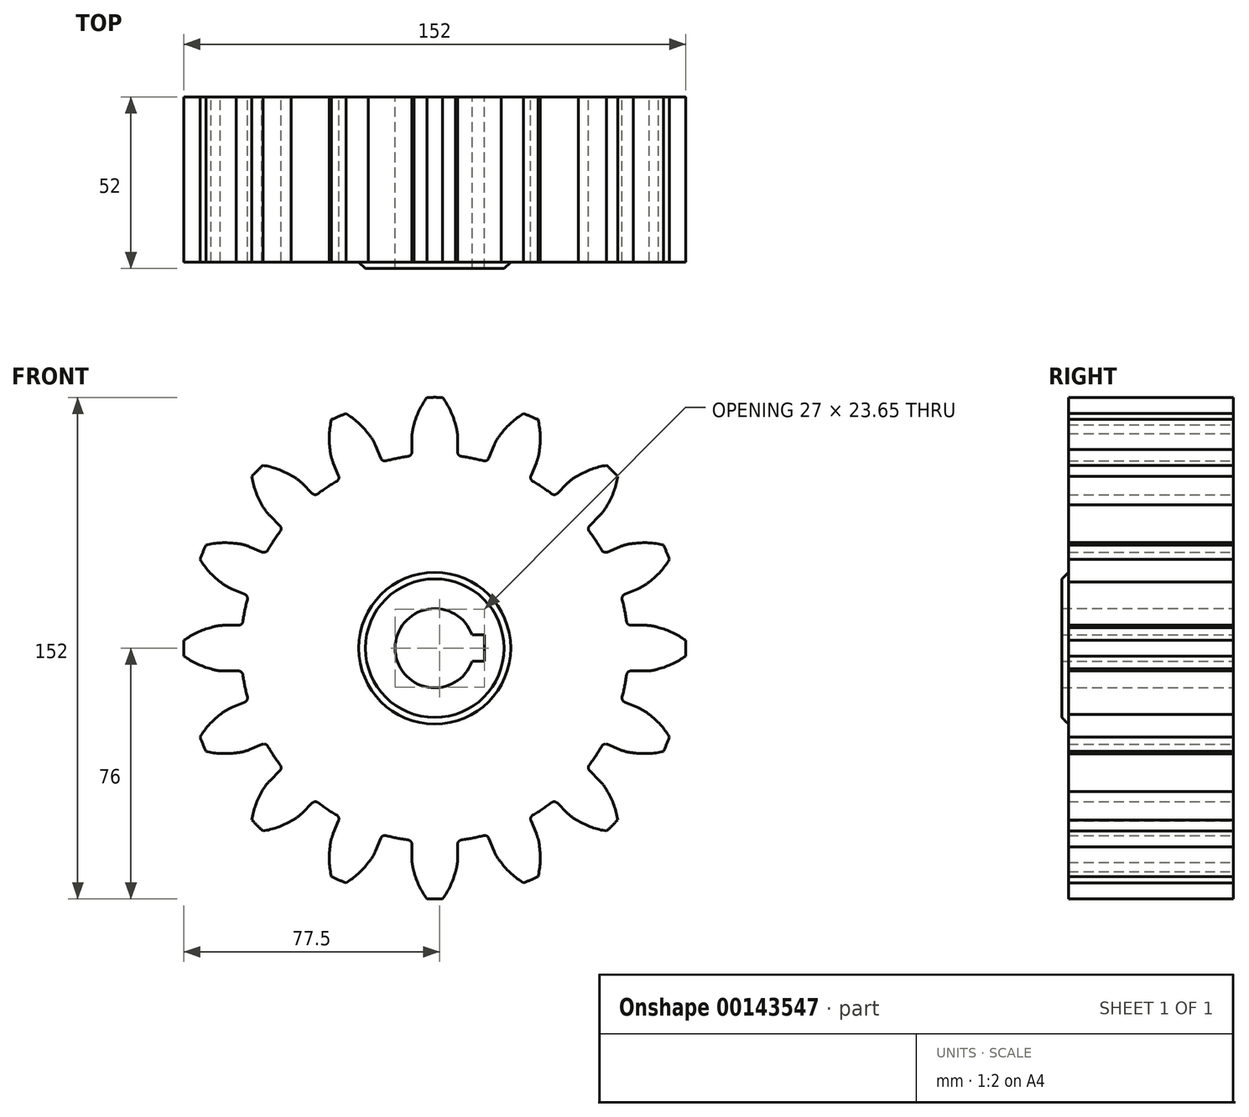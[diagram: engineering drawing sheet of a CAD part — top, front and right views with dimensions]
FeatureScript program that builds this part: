
annotation { "Feature Type Name" : "Feature", "Feature Type Description" : "" }
export const myFeature = defineFeature(function(context is Context, id is Id, definition is map)
    precondition{}
    {
        {
            var Q0;
            Q0=qCreatedBy(makeId("Front.planeOp"),FACE);
            var sketch = newSketch(context, id + "F0", { "sketchPlane" : qUnion([Q0])});
            skArc(sketch, "E0", {"start": v(-52.04, 55.39) * mm, "mid": v(-53.74, 53.74) * mm, "end": v(-55.39, 52.04) * mm});
            skArc(sketch, "E1", {"start": v(-8.06, 58.1) * mm, "mid": v(-11.44, 57.53) * mm, "end": v(-14.78, 56.77) * mm});
            skLineSegment(sketch, "E2", {"start": v(6.92, 59.42) * mm, "end": v(6.92, 63.63) * mm});
            skArc(sketch, "E3", {"start": v(6.92, 63.63) * mm, "mid": v(6.77, 65.7) * mm, "end": v(6.28, 67.7) * mm});
            skArc(sketch, "E4", {"start": v(6.28, 67.7) * mm, "mid": v(4.72, 72.02) * mm, "end": v(2.37, 75.96) * mm});
            skLineSegment(sketch, "E5", {"start": v(0, 0) * mm, "end": v(0, 104.76) * mm, "construction": true});
            skArc(sketch, "E6.MirrorCS", {"start": v(-6.28, 67.7) * mm, "mid": v(-4.72, 72.02) * mm, "end": v(-2.37, 75.96) * mm});
            skArc(sketch, "E7.MirrorCS", {"start": v(-6.92, 63.63) * mm, "mid": v(-6.77, 65.7) * mm, "end": v(-6.28, 67.7) * mm});
            skLineSegment(sketch, "E8.MirrorCS", {"start": v(-6.92, 59.42) * mm, "end": v(-6.92, 63.63) * mm});
            skPoint(sketch, "E9.visualSharp", {"position": v(6.92, 58.25) * mm});
            skArc(sketch, "E9.filletArc", {"start": v(6.92, 59.42) * mm, "mid": v(7.24, 58.55) * mm, "end": v(8.06, 58.1) * mm});
            skPoint(sketch, "E10.visualSharp", {"position": v(-6.92, 58.25) * mm});
            skArc(sketch, "E10.filletArc", {"start": v(-8.06, 58.1) * mm, "mid": v(-7.24, 58.55) * mm, "end": v(-6.92, 59.42) * mm});
            skArc(sketch, "E11.1.0", {"start": v(31.71, 60.15) * mm, "mid": v(31.92, 64.74) * mm, "end": v(31.26, 69.28) * mm});
            skArc(sketch, "E11.1.1", {"start": v(20.1, 64.96) * mm, "mid": v(23.2, 68.35) * mm, "end": v(26.88, 71.09) * mm});
            skArc(sketch, "E11.1.2", {"start": v(30.74, 56.13) * mm, "mid": v(31.4, 58.1) * mm, "end": v(31.71, 60.15) * mm});
            skArc(sketch, "E11.1.3", {"start": v(17.96, 61.43) * mm, "mid": v(18.89, 63.28) * mm, "end": v(20.1, 64.96) * mm});
            skLineSegment(sketch, "E11.1.4", {"start": v(16.35, 57.54) * mm, "end": v(17.96, 61.43) * mm});
            skLineSegment(sketch, "E11.1.5", {"start": v(29.13, 52.25) * mm, "end": v(30.74, 56.13) * mm});
            skArc(sketch, "E11.1.6", {"start": v(29.13, 52.25) * mm, "mid": v(29.1, 51.32) * mm, "end": v(29.69, 50.6) * mm});
            skArc(sketch, "E11.1.7", {"start": v(14.78, 56.77) * mm, "mid": v(15.71, 56.86) * mm, "end": v(16.35, 57.54) * mm});
            skArc(sketch, "E11.2.0", {"start": v(52.32, 43.44) * mm, "mid": v(54.26, 47.6) * mm, "end": v(55.39, 52.04) * mm});
            skArc(sketch, "E11.2.1", {"start": v(43.44, 52.32) * mm, "mid": v(47.6, 54.26) * mm, "end": v(52.04, 55.39) * mm});
            skArc(sketch, "E11.2.2", {"start": v(49.88, 40.1) * mm, "mid": v(51.24, 41.67) * mm, "end": v(52.32, 43.44) * mm});
            skArc(sketch, "E11.2.3", {"start": v(40.1, 49.88) * mm, "mid": v(41.67, 51.24) * mm, "end": v(43.44, 52.32) * mm});
            skLineSegment(sketch, "E11.2.4", {"start": v(37.13, 46.9) * mm, "end": v(40.1, 49.88) * mm});
            skLineSegment(sketch, "E11.2.5", {"start": v(46.9, 37.13) * mm, "end": v(49.88, 40.1) * mm});
            skArc(sketch, "E11.2.6", {"start": v(46.9, 37.13) * mm, "mid": v(46.52, 36.28) * mm, "end": v(46.79, 35.38) * mm});
            skArc(sketch, "E11.2.7", {"start": v(35.38, 46.79) * mm, "mid": v(36.28, 46.52) * mm, "end": v(37.13, 46.9) * mm});
            skArc(sketch, "E11.3.0", {"start": v(64.96, 20.1) * mm, "mid": v(68.35, 23.2) * mm, "end": v(71.09, 26.88) * mm});
            skArc(sketch, "E11.3.1", {"start": v(60.15, 31.71) * mm, "mid": v(64.74, 31.92) * mm, "end": v(69.28, 31.26) * mm});
            skArc(sketch, "E11.3.2", {"start": v(61.43, 17.96) * mm, "mid": v(63.28, 18.89) * mm, "end": v(64.96, 20.1) * mm});
            skArc(sketch, "E11.3.3", {"start": v(56.13, 30.74) * mm, "mid": v(58.1, 31.4) * mm, "end": v(60.15, 31.71) * mm});
            skLineSegment(sketch, "E11.3.4", {"start": v(52.25, 29.13) * mm, "end": v(56.13, 30.74) * mm});
            skLineSegment(sketch, "E11.3.5", {"start": v(57.54, 16.35) * mm, "end": v(61.43, 17.96) * mm});
            skArc(sketch, "E11.3.6", {"start": v(57.54, 16.35) * mm, "mid": v(56.86, 15.71) * mm, "end": v(56.77, 14.78) * mm});
            skArc(sketch, "E11.3.7", {"start": v(50.6, 29.69) * mm, "mid": v(51.32, 29.1) * mm, "end": v(52.25, 29.13) * mm});
            skArc(sketch, "E11.4.0", {"start": v(67.7, -6.28) * mm, "mid": v(72.02, -4.72) * mm, "end": v(75.96, -2.37) * mm});
            skArc(sketch, "E11.4.1", {"start": v(67.7, 6.28) * mm, "mid": v(72.02, 4.72) * mm, "end": v(75.96, 2.37) * mm});
            skArc(sketch, "E11.4.2", {"start": v(63.63, -6.92) * mm, "mid": v(65.7, -6.77) * mm, "end": v(67.7, -6.28) * mm});
            skArc(sketch, "E11.4.3", {"start": v(63.63, 6.92) * mm, "mid": v(65.7, 6.77) * mm, "end": v(67.7, 6.28) * mm});
            skLineSegment(sketch, "E11.4.4", {"start": v(59.42, 6.92) * mm, "end": v(63.63, 6.92) * mm});
            skLineSegment(sketch, "E11.4.5", {"start": v(59.42, -6.92) * mm, "end": v(63.63, -6.92) * mm});
            skArc(sketch, "E11.4.6", {"start": v(59.42, -6.92) * mm, "mid": v(58.55, -7.24) * mm, "end": v(58.1, -8.06) * mm});
            skArc(sketch, "E11.4.7", {"start": v(58.1, 8.06) * mm, "mid": v(58.55, 7.24) * mm, "end": v(59.42, 6.92) * mm});
            skArc(sketch, "E11.5.0", {"start": v(60.15, -31.71) * mm, "mid": v(64.74, -31.92) * mm, "end": v(69.28, -31.26) * mm});
            skArc(sketch, "E11.5.1", {"start": v(64.96, -20.1) * mm, "mid": v(68.35, -23.2) * mm, "end": v(71.09, -26.88) * mm});
            skArc(sketch, "E11.5.2", {"start": v(56.13, -30.74) * mm, "mid": v(58.1, -31.4) * mm, "end": v(60.15, -31.71) * mm});
            skArc(sketch, "E11.5.3", {"start": v(61.43, -17.96) * mm, "mid": v(63.28, -18.89) * mm, "end": v(64.96, -20.1) * mm});
            skLineSegment(sketch, "E11.5.4", {"start": v(57.54, -16.35) * mm, "end": v(61.43, -17.96) * mm});
            skLineSegment(sketch, "E11.5.5", {"start": v(52.25, -29.13) * mm, "end": v(56.13, -30.74) * mm});
            skArc(sketch, "E11.5.6", {"start": v(52.25, -29.13) * mm, "mid": v(51.32, -29.1) * mm, "end": v(50.6, -29.69) * mm});
            skArc(sketch, "E11.5.7", {"start": v(56.77, -14.78) * mm, "mid": v(56.86, -15.71) * mm, "end": v(57.54, -16.35) * mm});
            skArc(sketch, "E11.6.0", {"start": v(43.44, -52.32) * mm, "mid": v(47.6, -54.26) * mm, "end": v(52.04, -55.39) * mm});
            skArc(sketch, "E11.6.1", {"start": v(52.32, -43.44) * mm, "mid": v(54.26, -47.6) * mm, "end": v(55.39, -52.04) * mm});
            skArc(sketch, "E11.6.2", {"start": v(40.1, -49.88) * mm, "mid": v(41.67, -51.24) * mm, "end": v(43.44, -52.32) * mm});
            skArc(sketch, "E11.6.3", {"start": v(49.88, -40.1) * mm, "mid": v(51.24, -41.67) * mm, "end": v(52.32, -43.44) * mm});
            skLineSegment(sketch, "E11.6.4", {"start": v(46.9, -37.13) * mm, "end": v(49.88, -40.1) * mm});
            skLineSegment(sketch, "E11.6.5", {"start": v(37.13, -46.9) * mm, "end": v(40.1, -49.88) * mm});
            skArc(sketch, "E11.6.6", {"start": v(37.13, -46.9) * mm, "mid": v(36.28, -46.52) * mm, "end": v(35.38, -46.79) * mm});
            skArc(sketch, "E11.6.7", {"start": v(46.79, -35.38) * mm, "mid": v(46.52, -36.28) * mm, "end": v(46.9, -37.13) * mm});
            skArc(sketch, "E11.7.0", {"start": v(20.1, -64.96) * mm, "mid": v(23.2, -68.35) * mm, "end": v(26.88, -71.09) * mm});
            skArc(sketch, "E11.7.1", {"start": v(31.71, -60.15) * mm, "mid": v(31.92, -64.74) * mm, "end": v(31.26, -69.28) * mm});
            skArc(sketch, "E11.7.2", {"start": v(17.96, -61.43) * mm, "mid": v(18.89, -63.28) * mm, "end": v(20.1, -64.96) * mm});
            skArc(sketch, "E11.7.3", {"start": v(30.74, -56.13) * mm, "mid": v(31.4, -58.1) * mm, "end": v(31.71, -60.15) * mm});
            skLineSegment(sketch, "E11.7.4", {"start": v(29.13, -52.25) * mm, "end": v(30.74, -56.13) * mm});
            skLineSegment(sketch, "E11.7.5", {"start": v(16.35, -57.54) * mm, "end": v(17.96, -61.43) * mm});
            skArc(sketch, "E11.7.6", {"start": v(16.35, -57.54) * mm, "mid": v(15.71, -56.86) * mm, "end": v(14.78, -56.77) * mm});
            skArc(sketch, "E11.7.7", {"start": v(29.69, -50.6) * mm, "mid": v(29.1, -51.32) * mm, "end": v(29.13, -52.25) * mm});
            skArc(sketch, "E11.8.0", {"start": v(-6.28, -67.7) * mm, "mid": v(-4.72, -72.02) * mm, "end": v(-2.37, -75.96) * mm});
            skArc(sketch, "E11.8.1", {"start": v(6.28, -67.7) * mm, "mid": v(4.72, -72.02) * mm, "end": v(2.37, -75.96) * mm});
            skArc(sketch, "E11.8.2", {"start": v(-6.92, -63.63) * mm, "mid": v(-6.77, -65.7) * mm, "end": v(-6.28, -67.7) * mm});
            skArc(sketch, "E11.8.3", {"start": v(6.92, -63.63) * mm, "mid": v(6.77, -65.7) * mm, "end": v(6.28, -67.7) * mm});
            skLineSegment(sketch, "E11.8.4", {"start": v(6.92, -59.42) * mm, "end": v(6.92, -63.63) * mm});
            skLineSegment(sketch, "E11.8.5", {"start": v(-6.92, -59.42) * mm, "end": v(-6.92, -63.63) * mm});
            skArc(sketch, "E11.8.6", {"start": v(-6.92, -59.42) * mm, "mid": v(-7.24, -58.55) * mm, "end": v(-8.06, -58.1) * mm});
            skArc(sketch, "E11.8.7", {"start": v(8.06, -58.1) * mm, "mid": v(7.24, -58.55) * mm, "end": v(6.92, -59.42) * mm});
            skArc(sketch, "E11.9.0", {"start": v(-31.71, -60.15) * mm, "mid": v(-31.92, -64.74) * mm, "end": v(-31.26, -69.28) * mm});
            skArc(sketch, "E11.9.1", {"start": v(-20.1, -64.96) * mm, "mid": v(-23.2, -68.35) * mm, "end": v(-26.88, -71.09) * mm});
            skArc(sketch, "E11.9.2", {"start": v(-30.74, -56.13) * mm, "mid": v(-31.4, -58.1) * mm, "end": v(-31.71, -60.15) * mm});
            skArc(sketch, "E11.9.3", {"start": v(-17.96, -61.43) * mm, "mid": v(-18.89, -63.28) * mm, "end": v(-20.1, -64.96) * mm});
            skLineSegment(sketch, "E11.9.4", {"start": v(-16.35, -57.54) * mm, "end": v(-17.96, -61.43) * mm});
            skLineSegment(sketch, "E11.9.5", {"start": v(-29.13, -52.25) * mm, "end": v(-30.74, -56.13) * mm});
            skArc(sketch, "E11.9.6", {"start": v(-29.13, -52.25) * mm, "mid": v(-29.1, -51.32) * mm, "end": v(-29.69, -50.6) * mm});
            skArc(sketch, "E11.9.7", {"start": v(-14.78, -56.77) * mm, "mid": v(-15.71, -56.86) * mm, "end": v(-16.35, -57.54) * mm});
            skArc(sketch, "E11.10.0", {"start": v(-52.32, -43.44) * mm, "mid": v(-54.26, -47.6) * mm, "end": v(-55.39, -52.04) * mm});
            skArc(sketch, "E11.10.1", {"start": v(-43.44, -52.32) * mm, "mid": v(-47.6, -54.26) * mm, "end": v(-52.04, -55.39) * mm});
            skArc(sketch, "E11.10.2", {"start": v(-49.88, -40.1) * mm, "mid": v(-51.24, -41.67) * mm, "end": v(-52.32, -43.44) * mm});
            skArc(sketch, "E11.10.3", {"start": v(-40.1, -49.88) * mm, "mid": v(-41.67, -51.24) * mm, "end": v(-43.44, -52.32) * mm});
            skLineSegment(sketch, "E11.10.4", {"start": v(-37.13, -46.9) * mm, "end": v(-40.1, -49.88) * mm});
            skLineSegment(sketch, "E11.10.5", {"start": v(-46.9, -37.13) * mm, "end": v(-49.88, -40.1) * mm});
            skArc(sketch, "E11.10.6", {"start": v(-46.9, -37.13) * mm, "mid": v(-46.52, -36.28) * mm, "end": v(-46.79, -35.38) * mm});
            skArc(sketch, "E11.10.7", {"start": v(-35.38, -46.79) * mm, "mid": v(-36.28, -46.52) * mm, "end": v(-37.13, -46.9) * mm});
            skArc(sketch, "E11.11.0", {"start": v(-64.96, -20.1) * mm, "mid": v(-68.35, -23.2) * mm, "end": v(-71.09, -26.88) * mm});
            skArc(sketch, "E11.11.1", {"start": v(-60.15, -31.71) * mm, "mid": v(-64.74, -31.92) * mm, "end": v(-69.28, -31.26) * mm});
            skArc(sketch, "E11.11.2", {"start": v(-61.43, -17.96) * mm, "mid": v(-63.28, -18.89) * mm, "end": v(-64.96, -20.1) * mm});
            skArc(sketch, "E11.11.3", {"start": v(-56.13, -30.74) * mm, "mid": v(-58.1, -31.4) * mm, "end": v(-60.15, -31.71) * mm});
            skLineSegment(sketch, "E11.11.4", {"start": v(-52.25, -29.13) * mm, "end": v(-56.13, -30.74) * mm});
            skLineSegment(sketch, "E11.11.5", {"start": v(-57.54, -16.35) * mm, "end": v(-61.43, -17.96) * mm});
            skArc(sketch, "E11.11.6", {"start": v(-57.54, -16.35) * mm, "mid": v(-56.86, -15.71) * mm, "end": v(-56.77, -14.78) * mm});
            skArc(sketch, "E11.11.7", {"start": v(-50.6, -29.69) * mm, "mid": v(-51.32, -29.1) * mm, "end": v(-52.25, -29.13) * mm});
            skArc(sketch, "E11.12.0", {"start": v(-67.7, 6.28) * mm, "mid": v(-72.02, 4.72) * mm, "end": v(-75.96, 2.37) * mm});
            skArc(sketch, "E11.12.1", {"start": v(-67.7, -6.28) * mm, "mid": v(-72.02, -4.72) * mm, "end": v(-75.96, -2.37) * mm});
            skArc(sketch, "E11.12.2", {"start": v(-63.63, 6.92) * mm, "mid": v(-65.7, 6.77) * mm, "end": v(-67.7, 6.28) * mm});
            skArc(sketch, "E11.12.3", {"start": v(-63.63, -6.92) * mm, "mid": v(-65.7, -6.77) * mm, "end": v(-67.7, -6.28) * mm});
            skLineSegment(sketch, "E11.12.4", {"start": v(-59.42, -6.92) * mm, "end": v(-63.63, -6.92) * mm});
            skLineSegment(sketch, "E11.12.5", {"start": v(-59.42, 6.92) * mm, "end": v(-63.63, 6.92) * mm});
            skArc(sketch, "E11.12.6", {"start": v(-59.42, 6.92) * mm, "mid": v(-58.55, 7.24) * mm, "end": v(-58.1, 8.06) * mm});
            skArc(sketch, "E11.12.7", {"start": v(-58.1, -8.06) * mm, "mid": v(-58.55, -7.24) * mm, "end": v(-59.42, -6.92) * mm});
            skArc(sketch, "E11.13.0", {"start": v(-60.15, 31.71) * mm, "mid": v(-64.74, 31.92) * mm, "end": v(-69.28, 31.26) * mm});
            skArc(sketch, "E11.13.1", {"start": v(-64.96, 20.1) * mm, "mid": v(-68.35, 23.2) * mm, "end": v(-71.09, 26.88) * mm});
            skArc(sketch, "E11.13.2", {"start": v(-56.13, 30.74) * mm, "mid": v(-58.1, 31.4) * mm, "end": v(-60.15, 31.71) * mm});
            skArc(sketch, "E11.13.3", {"start": v(-61.43, 17.96) * mm, "mid": v(-63.28, 18.89) * mm, "end": v(-64.96, 20.1) * mm});
            skLineSegment(sketch, "E11.13.4", {"start": v(-57.54, 16.35) * mm, "end": v(-61.43, 17.96) * mm});
            skLineSegment(sketch, "E11.13.5", {"start": v(-52.25, 29.13) * mm, "end": v(-56.13, 30.74) * mm});
            skArc(sketch, "E11.13.6", {"start": v(-52.25, 29.13) * mm, "mid": v(-51.32, 29.1) * mm, "end": v(-50.6, 29.69) * mm});
            skArc(sketch, "E11.13.7", {"start": v(-56.77, 14.78) * mm, "mid": v(-56.86, 15.71) * mm, "end": v(-57.54, 16.35) * mm});
            skArc(sketch, "E11.14.0", {"start": v(-43.44, 52.32) * mm, "mid": v(-47.6, 54.26) * mm, "end": v(-52.04, 55.39) * mm});
            skArc(sketch, "E11.14.1", {"start": v(-52.32, 43.44) * mm, "mid": v(-54.26, 47.6) * mm, "end": v(-55.39, 52.04) * mm});
            skArc(sketch, "E11.14.2", {"start": v(-40.1, 49.88) * mm, "mid": v(-41.67, 51.24) * mm, "end": v(-43.44, 52.32) * mm});
            skArc(sketch, "E11.14.3", {"start": v(-49.88, 40.1) * mm, "mid": v(-51.24, 41.67) * mm, "end": v(-52.32, 43.44) * mm});
            skLineSegment(sketch, "E11.14.4", {"start": v(-46.9, 37.13) * mm, "end": v(-49.88, 40.1) * mm});
            skLineSegment(sketch, "E11.14.5", {"start": v(-37.13, 46.9) * mm, "end": v(-40.1, 49.88) * mm});
            skArc(sketch, "E11.14.6", {"start": v(-37.13, 46.9) * mm, "mid": v(-36.28, 46.52) * mm, "end": v(-35.38, 46.79) * mm});
            skArc(sketch, "E11.14.7", {"start": v(-46.79, 35.38) * mm, "mid": v(-46.52, 36.28) * mm, "end": v(-46.9, 37.13) * mm});
            skArc(sketch, "E11.15.0", {"start": v(-20.1, 64.96) * mm, "mid": v(-23.2, 68.35) * mm, "end": v(-26.88, 71.09) * mm});
            skArc(sketch, "E11.15.1", {"start": v(-31.71, 60.15) * mm, "mid": v(-31.92, 64.74) * mm, "end": v(-31.26, 69.28) * mm});
            skArc(sketch, "E11.15.2", {"start": v(-17.96, 61.43) * mm, "mid": v(-18.89, 63.28) * mm, "end": v(-20.1, 64.96) * mm});
            skArc(sketch, "E11.15.3", {"start": v(-30.74, 56.13) * mm, "mid": v(-31.4, 58.1) * mm, "end": v(-31.71, 60.15) * mm});
            skLineSegment(sketch, "E11.15.4", {"start": v(-29.13, 52.25) * mm, "end": v(-30.74, 56.13) * mm});
            skLineSegment(sketch, "E11.15.5", {"start": v(-16.35, 57.54) * mm, "end": v(-17.96, 61.43) * mm});
            skArc(sketch, "E11.15.6", {"start": v(-16.35, 57.54) * mm, "mid": v(-15.71, 56.86) * mm, "end": v(-14.78, 56.77) * mm});
            skArc(sketch, "E11.15.7", {"start": v(-29.69, 50.6) * mm, "mid": v(-29.1, 51.32) * mm, "end": v(-29.13, 52.25) * mm});
            skLineSegment(sketch, "E11.anchor1", {"start": v(0, 0) * mm, "end": v(-8.06, 58.1) * mm, "construction": true});
            skLineSegment(sketch, "E11.anchor2", {"start": v(0, 0) * mm, "end": v(-8.06, 58.1) * mm, "construction": true});
            skArc(sketch, "E12.trimOffspring", {"start": v(-29.69, 50.6) * mm, "mid": v(-32.59, 48.77) * mm, "end": v(-35.38, 46.79) * mm});
            skArc(sketch, "E13.trimOffspring", {"start": v(14.78, 56.77) * mm, "mid": v(11.44, 57.53) * mm, "end": v(8.06, 58.1) * mm});
            skArc(sketch, "E14.trimOffspring", {"start": v(35.38, 46.79) * mm, "mid": v(32.59, 48.77) * mm, "end": v(29.69, 50.6) * mm});
            skArc(sketch, "E15.trimOffspring", {"start": v(-46.79, 35.38) * mm, "mid": v(-48.77, 32.59) * mm, "end": v(-50.6, 29.69) * mm});
            skArc(sketch, "E16.trimOffspring", {"start": v(50.6, 29.69) * mm, "mid": v(48.77, 32.59) * mm, "end": v(46.79, 35.38) * mm});
            skArc(sketch, "E17.trimOffspring", {"start": v(58.1, 8.06) * mm, "mid": v(57.53, 11.44) * mm, "end": v(56.77, 14.78) * mm});
            skArc(sketch, "E18.trimOffspring", {"start": v(56.77, -14.78) * mm, "mid": v(57.53, -11.44) * mm, "end": v(58.1, -8.06) * mm});
            skArc(sketch, "E19.trimOffspring", {"start": v(-56.77, 14.78) * mm, "mid": v(-57.53, 11.44) * mm, "end": v(-58.1, 8.06) * mm});
            skArc(sketch, "E20.trimOffspring", {"start": v(-58.1, -8.06) * mm, "mid": v(-57.53, -11.44) * mm, "end": v(-56.77, -14.78) * mm});
            skArc(sketch, "E21.trimOffspring", {"start": v(-50.6, -29.69) * mm, "mid": v(-48.77, -32.59) * mm, "end": v(-46.79, -35.38) * mm});
            skArc(sketch, "E22.trimOffspring", {"start": v(-35.38, -46.79) * mm, "mid": v(-32.59, -48.77) * mm, "end": v(-29.69, -50.6) * mm});
            skArc(sketch, "E23.trimOffspring", {"start": v(-14.78, -56.77) * mm, "mid": v(-11.44, -57.53) * mm, "end": v(-8.06, -58.1) * mm});
            skArc(sketch, "E24.trimOffspring", {"start": v(8.06, -58.1) * mm, "mid": v(11.44, -57.53) * mm, "end": v(14.78, -56.77) * mm});
            skArc(sketch, "E25.trimOffspring", {"start": v(29.69, -50.6) * mm, "mid": v(32.59, -48.77) * mm, "end": v(35.38, -46.79) * mm});
            skArc(sketch, "E26.trimOffspring", {"start": v(46.79, -35.38) * mm, "mid": v(48.77, -32.59) * mm, "end": v(50.6, -29.69) * mm});
            skArc(sketch, "E27.trimOffspring", {"start": v(-26.88, 71.09) * mm, "mid": v(-29.08, 70.21) * mm, "end": v(-31.26, 69.28) * mm});
            skArc(sketch, "E28.trimOffspring", {"start": v(-75.96, 2.37) * mm, "mid": v(-76, 0) * mm, "end": v(-75.96, -2.37) * mm});
            skArc(sketch, "E29.trimOffspring", {"start": v(-55.39, -52.04) * mm, "mid": v(-53.74, -53.74) * mm, "end": v(-52.04, -55.39) * mm});
            skArc(sketch, "E30.trimOffspring", {"start": v(-71.09, -26.88) * mm, "mid": v(-70.21, -29.08) * mm, "end": v(-69.28, -31.26) * mm});
            skArc(sketch, "E31.trimOffspring", {"start": v(-2.37, -75.96) * mm, "mid": v(0, -76) * mm, "end": v(2.37, -75.96) * mm});
            skArc(sketch, "E32.trimOffspring", {"start": v(52.04, -55.39) * mm, "mid": v(53.74, -53.74) * mm, "end": v(55.39, -52.04) * mm});
            skArc(sketch, "E33.trimOffspring", {"start": v(26.88, -71.09) * mm, "mid": v(29.08, -70.21) * mm, "end": v(31.26, -69.28) * mm});
            skArc(sketch, "E34.trimOffspring", {"start": v(75.96, -2.37) * mm, "mid": v(76, 0) * mm, "end": v(75.96, 2.37) * mm});
            skArc(sketch, "E35.trimOffspring", {"start": v(55.39, 52.04) * mm, "mid": v(53.74, 53.74) * mm, "end": v(52.04, 55.39) * mm});
            skArc(sketch, "E36.trimOffspring", {"start": v(2.37, 75.96) * mm, "mid": v(0, 76) * mm, "end": v(-2.37, 75.96) * mm});
            skArc(sketch, "E37.trimOffspring", {"start": v(31.26, 69.28) * mm, "mid": v(29.08, 70.21) * mm, "end": v(26.88, 71.09) * mm});
            skArc(sketch, "E38", {"start": v(71.09, 26.88) * mm, "mid": v(70.21, 29.08) * mm, "end": v(69.28, 31.26) * mm});
            skArc(sketch, "E39", {"start": v(69.28, -31.26) * mm, "mid": v(70.21, -29.08) * mm, "end": v(71.09, -26.88) * mm});
            skArc(sketch, "E40", {"start": v(-69.28, 31.26) * mm, "mid": v(-70.21, 29.08) * mm, "end": v(-71.09, 26.88) * mm});
            skArc(sketch, "E41", {"start": v(-26.88, -71.09) * mm, "mid": v(-29.08, -70.21) * mm, "end": v(-31.26, -69.28) * mm});
            skArc(sketch, "E42", {"start": v(11.31, 4) * mm, "mid": v(-12, 0) * mm, "end": v(11.31, -4) * mm});
            skLineSegment(sketch, "E43", {"start": v(-12, 0) * mm, "end": v(0, 0) * mm});
            skLineSegment(sketch, "E44", {"start": v(15, 0) * mm, "end": v(15, 4) * mm});
            skLineSegment(sketch, "E45", {"start": v(15, 4) * mm, "end": v(11.31, 4) * mm});
            skLineSegment(sketch, "E46", {"start": v(15, 0) * mm, "end": v(15, -4) * mm});
            skLineSegment(sketch, "E47", {"start": v(15, -4) * mm, "end": v(11.31, -4) * mm});
            skSolve(sketch);
        }
        {
            var Q0;
            Q0 = qSketchRegion(id + "F0", true);
            extrude(context, id + "F1", {"entities" : qUnion([Q0]), "endBound" : BoundingType.SYMMETRIC, "depth" : 50 * mm});
        }
        {
            var Q0;
            Q0=makeQuery(id+"F1.opExtrude","CAP_FACE",FACE,{"disambiguationData":[OSD([sQuery(id+"F0.wireOp",EDGE,"E0"),sQuery(id+"F0.wireOp",EDGE,"E1"),sQuery(id+"F0.wireOp",EDGE,"E11.1.0"),sQuery(id+"F0.wireOp",EDGE,"E11.1.1"),sQuery(id+"F0.wireOp",EDGE,"E11.1.2"),sQuery(id+"F0.wireOp",EDGE,"E11.1.3"),sQuery(id+"F0.wireOp",EDGE,"E11.1.4"),sQuery(id+"F0.wireOp",EDGE,"E11.1.5"),sQuery(id+"F0.wireOp",EDGE,"E11.1.6"),sQuery(id+"F0.wireOp",EDGE,"E11.1.7"),sQuery(id+"F0.wireOp",EDGE,"E11.2.0"),sQuery(id+"F0.wireOp",EDGE,"E11.2.1"),sQuery(id+"F0.wireOp",EDGE,"E11.2.2"),sQuery(id+"F0.wireOp",EDGE,"E11.2.3"),sQuery(id+"F0.wireOp",EDGE,"E11.2.4"),sQuery(id+"F0.wireOp",EDGE,"E11.2.5"),sQuery(id+"F0.wireOp",EDGE,"E11.2.6"),sQuery(id+"F0.wireOp",EDGE,"E11.2.7"),sQuery(id+"F0.wireOp",EDGE,"E11.3.0"),sQuery(id+"F0.wireOp",EDGE,"E11.3.1"),sQuery(id+"F0.wireOp",EDGE,"E11.3.2"),sQuery(id+"F0.wireOp",EDGE,"E11.3.3"),sQuery(id+"F0.wireOp",EDGE,"E11.3.4"),sQuery(id+"F0.wireOp",EDGE,"E11.3.5"),sQuery(id+"F0.wireOp",EDGE,"E11.3.6"),sQuery(id+"F0.wireOp",EDGE,"E11.3.7"),sQuery(id+"F0.wireOp",EDGE,"E11.4.0"),sQuery(id+"F0.wireOp",EDGE,"E11.4.1"),sQuery(id+"F0.wireOp",EDGE,"E11.4.2"),sQuery(id+"F0.wireOp",EDGE,"E11.4.3"),sQuery(id+"F0.wireOp",EDGE,"E11.4.4"),sQuery(id+"F0.wireOp",EDGE,"E11.4.5"),sQuery(id+"F0.wireOp",EDGE,"E11.4.6"),sQuery(id+"F0.wireOp",EDGE,"E11.4.7"),sQuery(id+"F0.wireOp",EDGE,"E11.5.0"),sQuery(id+"F0.wireOp",EDGE,"E11.5.1"),sQuery(id+"F0.wireOp",EDGE,"E11.5.2"),sQuery(id+"F0.wireOp",EDGE,"E11.5.3"),sQuery(id+"F0.wireOp",EDGE,"E11.5.4"),sQuery(id+"F0.wireOp",EDGE,"E11.5.5"),sQuery(id+"F0.wireOp",EDGE,"E11.5.6"),sQuery(id+"F0.wireOp",EDGE,"E11.5.7"),sQuery(id+"F0.wireOp",EDGE,"E11.6.0"),sQuery(id+"F0.wireOp",EDGE,"E11.6.1"),sQuery(id+"F0.wireOp",EDGE,"E11.6.2"),sQuery(id+"F0.wireOp",EDGE,"E11.6.3"),sQuery(id+"F0.wireOp",EDGE,"E11.6.4"),sQuery(id+"F0.wireOp",EDGE,"E11.6.5"),sQuery(id+"F0.wireOp",EDGE,"E11.6.6"),sQuery(id+"F0.wireOp",EDGE,"E11.6.7"),sQuery(id+"F0.wireOp",EDGE,"E11.7.0"),sQuery(id+"F0.wireOp",EDGE,"E11.7.1"),sQuery(id+"F0.wireOp",EDGE,"E11.7.2"),sQuery(id+"F0.wireOp",EDGE,"E11.7.3"),sQuery(id+"F0.wireOp",EDGE,"E11.7.4"),sQuery(id+"F0.wireOp",EDGE,"E11.7.5"),sQuery(id+"F0.wireOp",EDGE,"E11.7.6"),sQuery(id+"F0.wireOp",EDGE,"E11.7.7"),sQuery(id+"F0.wireOp",EDGE,"E11.8.0"),sQuery(id+"F0.wireOp",EDGE,"E11.8.1"),sQuery(id+"F0.wireOp",EDGE,"E11.8.2"),sQuery(id+"F0.wireOp",EDGE,"E11.8.3"),sQuery(id+"F0.wireOp",EDGE,"E11.8.4"),sQuery(id+"F0.wireOp",EDGE,"E11.8.5"),sQuery(id+"F0.wireOp",EDGE,"E11.8.6"),sQuery(id+"F0.wireOp",EDGE,"E11.8.7"),sQuery(id+"F0.wireOp",EDGE,"E11.9.0"),sQuery(id+"F0.wireOp",EDGE,"E11.9.1"),sQuery(id+"F0.wireOp",EDGE,"E11.9.2"),sQuery(id+"F0.wireOp",EDGE,"E11.9.3"),sQuery(id+"F0.wireOp",EDGE,"E11.9.4"),sQuery(id+"F0.wireOp",EDGE,"E11.9.5"),sQuery(id+"F0.wireOp",EDGE,"E11.9.6"),sQuery(id+"F0.wireOp",EDGE,"E11.9.7"),sQuery(id+"F0.wireOp",EDGE,"E11.10.0"),sQuery(id+"F0.wireOp",EDGE,"E11.10.1"),sQuery(id+"F0.wireOp",EDGE,"E11.10.2"),sQuery(id+"F0.wireOp",EDGE,"E11.10.3"),sQuery(id+"F0.wireOp",EDGE,"E11.10.4"),sQuery(id+"F0.wireOp",EDGE,"E11.10.5"),sQuery(id+"F0.wireOp",EDGE,"E11.10.6"),sQuery(id+"F0.wireOp",EDGE,"E11.10.7"),sQuery(id+"F0.wireOp",EDGE,"E11.11.0"),sQuery(id+"F0.wireOp",EDGE,"E11.11.1"),sQuery(id+"F0.wireOp",EDGE,"E11.11.2"),sQuery(id+"F0.wireOp",EDGE,"E11.11.3"),sQuery(id+"F0.wireOp",EDGE,"E11.11.4"),sQuery(id+"F0.wireOp",EDGE,"E11.11.5"),sQuery(id+"F0.wireOp",EDGE,"E11.11.6"),sQuery(id+"F0.wireOp",EDGE,"E11.11.7"),sQuery(id+"F0.wireOp",EDGE,"E11.12.0"),sQuery(id+"F0.wireOp",EDGE,"E11.12.1"),sQuery(id+"F0.wireOp",EDGE,"E11.12.2"),sQuery(id+"F0.wireOp",EDGE,"E11.12.3"),sQuery(id+"F0.wireOp",EDGE,"E11.12.4"),sQuery(id+"F0.wireOp",EDGE,"E11.12.5"),sQuery(id+"F0.wireOp",EDGE,"E11.12.6"),sQuery(id+"F0.wireOp",EDGE,"E11.12.7"),sQuery(id+"F0.wireOp",EDGE,"E11.13.0"),sQuery(id+"F0.wireOp",EDGE,"E11.13.1"),sQuery(id+"F0.wireOp",EDGE,"E11.13.2"),sQuery(id+"F0.wireOp",EDGE,"E11.13.3"),sQuery(id+"F0.wireOp",EDGE,"E11.13.4"),sQuery(id+"F0.wireOp",EDGE,"E11.13.5"),sQuery(id+"F0.wireOp",EDGE,"E11.13.6"),sQuery(id+"F0.wireOp",EDGE,"E11.13.7"),sQuery(id+"F0.wireOp",EDGE,"E11.14.0"),sQuery(id+"F0.wireOp",EDGE,"E11.14.1"),sQuery(id+"F0.wireOp",EDGE,"E11.14.2"),sQuery(id+"F0.wireOp",EDGE,"E11.14.3"),sQuery(id+"F0.wireOp",EDGE,"E11.14.4"),sQuery(id+"F0.wireOp",EDGE,"E11.14.5"),sQuery(id+"F0.wireOp",EDGE,"E11.14.6"),sQuery(id+"F0.wireOp",EDGE,"E11.14.7"),sQuery(id+"F0.wireOp",EDGE,"E11.15.0"),sQuery(id+"F0.wireOp",EDGE,"E11.15.1"),sQuery(id+"F0.wireOp",EDGE,"E11.15.2"),sQuery(id+"F0.wireOp",EDGE,"E11.15.3"),sQuery(id+"F0.wireOp",EDGE,"E11.15.4"),sQuery(id+"F0.wireOp",EDGE,"E11.15.5"),sQuery(id+"F0.wireOp",EDGE,"E11.15.6"),sQuery(id+"F0.wireOp",EDGE,"E11.15.7"),sQuery(id+"F0.wireOp",EDGE,"E4"),sQuery(id+"F0.wireOp",EDGE,"E6.MirrorCS"),sQuery(id+"F0.wireOp",EDGE,"E3"),sQuery(id+"F0.wireOp",EDGE,"E7.MirrorCS"),sQuery(id+"F0.wireOp",EDGE,"E8.MirrorCS"),sQuery(id+"F0.wireOp",EDGE,"E2"),sQuery(id+"F0.wireOp",EDGE,"E9.filletArc"),sQuery(id+"F0.wireOp",EDGE,"E10.filletArc"),sQuery(id+"F0.wireOp",EDGE,"E12.trimOffspring"),sQuery(id+"F0.wireOp",EDGE,"E13.trimOffspring"),sQuery(id+"F0.wireOp",EDGE,"E14.trimOffspring"),sQuery(id+"F0.wireOp",EDGE,"E15.trimOffspring"),sQuery(id+"F0.wireOp",EDGE,"E16.trimOffspring"),sQuery(id+"F0.wireOp",EDGE,"E17.trimOffspring"),sQuery(id+"F0.wireOp",EDGE,"E18.trimOffspring"),sQuery(id+"F0.wireOp",EDGE,"E19.trimOffspring"),sQuery(id+"F0.wireOp",EDGE,"E20.trimOffspring"),sQuery(id+"F0.wireOp",EDGE,"E21.trimOffspring"),sQuery(id+"F0.wireOp",EDGE,"E22.trimOffspring"),sQuery(id+"F0.wireOp",EDGE,"E23.trimOffspring"),sQuery(id+"F0.wireOp",EDGE,"E24.trimOffspring"),sQuery(id+"F0.wireOp",EDGE,"E25.trimOffspring"),sQuery(id+"F0.wireOp",EDGE,"E26.trimOffspring"),sQuery(id+"F0.wireOp",EDGE,"E27.trimOffspring"),sQuery(id+"F0.wireOp",EDGE,"E28.trimOffspring"),sQuery(id+"F0.wireOp",EDGE,"E29.trimOffspring"),sQuery(id+"F0.wireOp",EDGE,"E30.trimOffspring"),sQuery(id+"F0.wireOp",EDGE,"E31.trimOffspring"),sQuery(id+"F0.wireOp",EDGE,"E32.trimOffspring"),sQuery(id+"F0.wireOp",EDGE,"E33.trimOffspring"),sQuery(id+"F0.wireOp",EDGE,"E34.trimOffspring"),sQuery(id+"F0.wireOp",EDGE,"E35.trimOffspring"),sQuery(id+"F0.wireOp",EDGE,"E36.trimOffspring"),sQuery(id+"F0.wireOp",EDGE,"E37.trimOffspring"),sQuery(id+"F0.wireOp",EDGE,"E38"),sQuery(id+"F0.wireOp",EDGE,"E39"),sQuery(id+"F0.wireOp",EDGE,"E40"),sQuery(id+"F0.wireOp",EDGE,"E41"),sQuery(id+"F0.wireOp",EDGE,"E42"),sQuery(id+"F0.wireOp",EDGE,"E44"),sQuery(id+"F0.wireOp",EDGE,"E45"),sQuery(id+"F0.wireOp",EDGE,"E46"),sQuery(id+"F0.wireOp",EDGE,"E47")])],"isStart":false});
            var sketch = newSketch(context, id + "F2", { "sketchPlane" : qUnion([Q0])});
            skCircle(sketch, "E48", {"center": v(0, 0) * mm, "radius": 23 * mm});
            skArc(sketch, "E49.0", {"start": v(11.31, 4) * mm, "mid": v(-12, 0) * mm, "end": v(11.31, -4) * mm});
            skLineSegment(sketch, "E50.0", {"start": v(15, 4) * mm, "end": v(11.31, 4) * mm});
            skLineSegment(sketch, "E50.1", {"start": v(15, -4) * mm, "end": v(15, 4) * mm});
            skLineSegment(sketch, "E50.2", {"start": v(15, -4) * mm, "end": v(11.31, -4) * mm});
            skSolve(sketch);
        }
        {
            var Q0;
            Q0 = qSketchRegion(id + "F2", true);
            extrude(context, id + "F3", {"entities" : qUnion([Q0]), "operationType" : NewBodyOperationType.ADD, "depth" : 2 * mm});
        }
        {
            var Q0;
            Q0=makeQuery(id+"F3.opExtrude","CAP_EDGE",EDGE,{"disambiguationData":[OSD([sQuery(id+"F2.wireOp",EDGE,"E48")])],"isStart":false});
            chamfer(context, id + "F4", {"entities" : qUnion([Q0]), "width" : 2 * mm, "tangentPropagation" : true});
        }
    });
